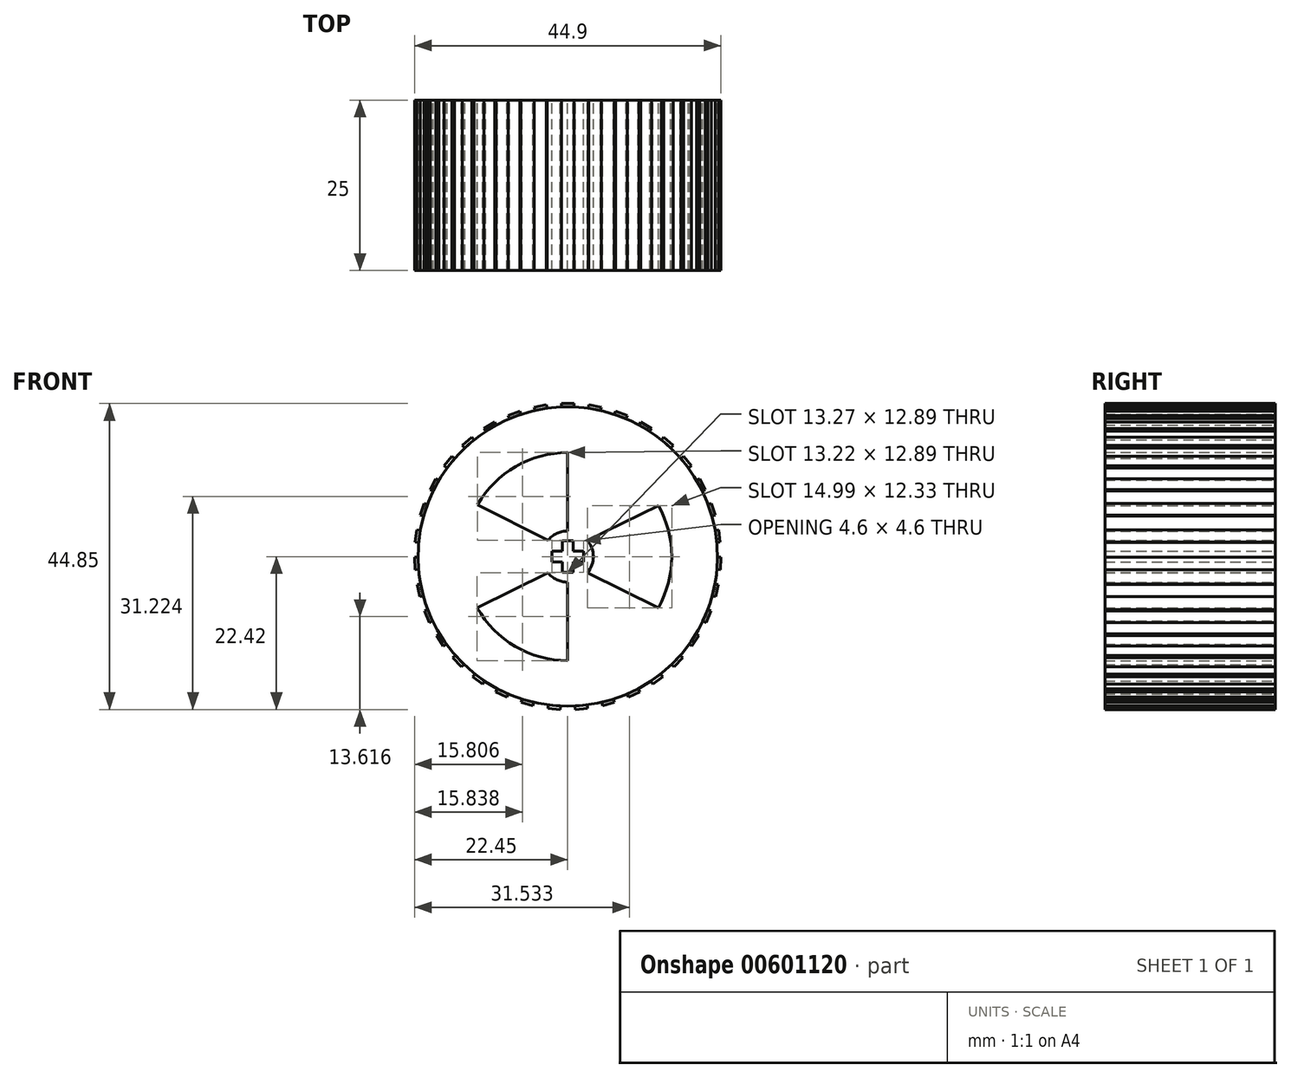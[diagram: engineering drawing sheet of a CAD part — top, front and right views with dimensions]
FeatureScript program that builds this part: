
annotation { "Feature Type Name" : "Feature", "Feature Type Description" : "" }
export const myFeature = defineFeature(function(context is Context, id is Id, definition is map)
    precondition{}
    {
        {
            var Q0;
            Q0=qCreatedBy(makeId("Front.planeOp"),FACE);
            var sketch = newSketch(context, id + "F0", { "sketchPlane" : qUnion([Q0])});
            skCircle(sketch, "E0", {"center": v(0, 0) * mm, "radius": 15.25 * mm});
            skCircle(sketch, "E1", {"center": v(0, 0) * mm, "radius": 21.95 * mm});
            skCircle(sketch, "E2", {"center": v(0, 0) * mm, "radius": 3.75 * mm});
            skLineSegment(sketch, "E3", {"start": v(-13.28, 7.62) * mm, "end": v(-2.92, 2.36) * mm});
            skLineSegment(sketch, "E4", {"start": v(-13.28, -7.5) * mm, "end": v(-2.92, -2.36) * mm});
            skLineSegment(sketch, "E5", {"start": v(13.28, -7.5) * mm, "end": v(2.92, -2.36) * mm});
            skLineSegment(sketch, "E6", {"start": v(2.92, 2.36) * mm, "end": v(13.28, 7.5) * mm});
            skLineSegment(sketch, "E7", {"start": v(0, 3.75) * mm, "end": v(0, 15.25) * mm});
            skLineSegment(sketch, "E8", {"start": v(0, -3.75) * mm, "end": v(0, -15.25) * mm});
            skLineSegment(sketch, "E9", {"start": v(0, 0) * mm, "end": v(0, 2.3) * mm});
            skLineSegment(sketch, "E10", {"start": v(0, 0) * mm, "end": v(2.3, 0) * mm});
            skLineSegment(sketch, "E11", {"start": v(0, 0) * mm, "end": v(0, -2.3) * mm});
            skLineSegment(sketch, "E12", {"start": v(0, 0) * mm, "end": v(-2.3, 0) * mm});
            skLineSegment(sketch, "E13", {"start": v(0, -2.3) * mm, "end": v(0.8, -2.3) * mm});
            skLineSegment(sketch, "E14", {"start": v(0, -2.3) * mm, "end": v(-0.8, -2.3) * mm});
            skLineSegment(sketch, "E15", {"start": v(2.3, 0) * mm, "end": v(2.3, 0.8) * mm});
            skLineSegment(sketch, "E16", {"start": v(2.3, 0) * mm, "end": v(2.3, -0.8) * mm});
            skLineSegment(sketch, "E17", {"start": v(-2.3, 0) * mm, "end": v(-2.3, 0.8) * mm});
            skLineSegment(sketch, "E18", {"start": v(-2.3, 0) * mm, "end": v(-2.3, -0.8) * mm});
            skLineSegment(sketch, "E19", {"start": v(0, 2.3) * mm, "end": v(0.8, 2.3) * mm});
            skLineSegment(sketch, "E20", {"start": v(0, 2.3) * mm, "end": v(-0.8, 2.3) * mm});
            skLineSegment(sketch, "E21", {"start": v(0.8, 0.8) * mm, "end": v(2.3, 0.8) * mm});
            skLineSegment(sketch, "E22", {"start": v(0.8, 2.3) * mm, "end": v(0.8, 0.8) * mm});
            skLineSegment(sketch, "E23", {"start": v(-0.8, 2.3) * mm, "end": v(-0.8, 0.8) * mm});
            skLineSegment(sketch, "E24", {"start": v(-2.3, 0.8) * mm, "end": v(-0.8, 0.8) * mm});
            skLineSegment(sketch, "E25", {"start": v(-2.3, -0.8) * mm, "end": v(-0.8, -0.8) * mm});
            skLineSegment(sketch, "E26", {"start": v(-0.8, -0.8) * mm, "end": v(-0.8, -2.3) * mm});
            skLineSegment(sketch, "E27", {"start": v(0.8, -2.3) * mm, "end": v(0.8, -0.8) * mm});
            skLineSegment(sketch, "E28", {"start": v(0.8, -0.8) * mm, "end": v(2.3, -0.8) * mm});
            skCircle(sketch, "E29", {"center": v(0, 0) * mm, "radius": 20 * mm});
            skLineSegment(sketch, "E30", {"start": v(0, 21.95) * mm, "end": v(-0.9, 21.93) * mm});
            skLineSegment(sketch, "E31", {"start": v(-0.9, 21.93) * mm, "end": v(0.9, 21.93) * mm});
            skLineSegment(sketch, "E32", {"start": v(0.9, 21.93) * mm, "end": v(0.9, 22.4) * mm});
            skLineSegment(sketch, "E33", {"start": v(0.9, 22.4) * mm, "end": v(-0.9, 22.4) * mm});
            skLineSegment(sketch, "E34", {"start": v(-0.9, 22.4) * mm, "end": v(-0.9, 21.93) * mm});
            skSolve(sketch);
        }
        {
            var Q0;
            Q0=makeQuery(id+"F0.imprint","IMPRINT",FACE,{"disambiguationData":[TD([[makeQuery(id+"F0.imprint","IMPRINT",EDGE,{"derivedFrom":sQuery(id+"F0.wireOp",EDGE,"E29")}),1.0]])]});
            var Q1;
            Q1=makeQuery(id+"F0.imprint","IMPRINT",FACE,{"disambiguationData":[TD([[makeQuery(id+"F0.imprint","IMPRINT",EDGE,{"derivedFrom":sQuery(id+"F0.wireOp",EDGE,"E29")}),-1.0]])]});
            var Q2;
            {var subQ0=sQuery(id+"F0.wireOp",EDGE,"E4");Q2=makeQuery(id+"F0.imprint","IMPRINT",FACE,{"disambiguationData":[TD([[makeQuery(id+"F0.imprint","IMPRINT",EDGE,{"derivedFrom":subQ0}),1.0]])]});}
            var Q3;
            {var subQ0=sQuery(id+"F0.wireOp",EDGE,"E5");Q3=makeQuery(id+"F0.imprint","IMPRINT",FACE,{"disambiguationData":[TD([[makeQuery(id+"F0.imprint","IMPRINT",EDGE,{"derivedFrom":subQ0}),1.0]])]});}
            var Q4;
            {var subQ0=sQuery(id+"F0.wireOp",EDGE,"E6");Q4=makeQuery(id+"F0.imprint","IMPRINT",FACE,{"disambiguationData":[TD([[makeQuery(id+"F0.imprint","IMPRINT",EDGE,{"derivedFrom":subQ0}),1.0]])]});}
            var Q5;
            Q5=makeQuery(id+"F0.imprint","IMPRINT",FACE,{"disambiguationData":[TD([[makeQuery(id+"F0.imprint","IMPRINT",EDGE,{"derivedFrom":sQuery(id+"F0.wireOp",EDGE,"E13")}),-1.0]])]});
            extrude(context, id + "F1", {"entities" : qUnion([Q0, Q1, Q2, Q3, Q4, Q5]), "depth" : 25 * mm, "offsetDistance" : 25 * mm});
        }
        {
            var Q0;
            Q0=makeQuery(id+"F1.opExtrude","SWEPT_FACE",FACE,{"disambiguationData":[OSD([sQuery(id+"F0.wireOp",EDGE,"E31")])]});
            extrude(context, id + "F2", {"entities" : qUnion([Q0]), "depth" : 0.5 * mm, "offsetDistance" : 25 * mm});
        }
        {
            var Q0;
            Q0=makeQuery(id+"F2.opExtrude","SWEPT_BODY",BODY,{"disambiguationData":[OSD([sQuery(id+"F0.wireOp",EDGE,"E31")])]});
            var Q1;
            Q1=makeQuery(id+"F1.opExtrude","SWEPT_FACE",FACE,{"disambiguationData":[OSD([sQuery(id+"F0.wireOp",EDGE,"E1")])]});
            circularPattern(context, id + "F3", {"entities" : qUnion([Q0]), "axis" : qUnion([Q1]), "angle" : 360 * degree, "instanceCount" : 35, "equalSpace" : true});
        }
    });
